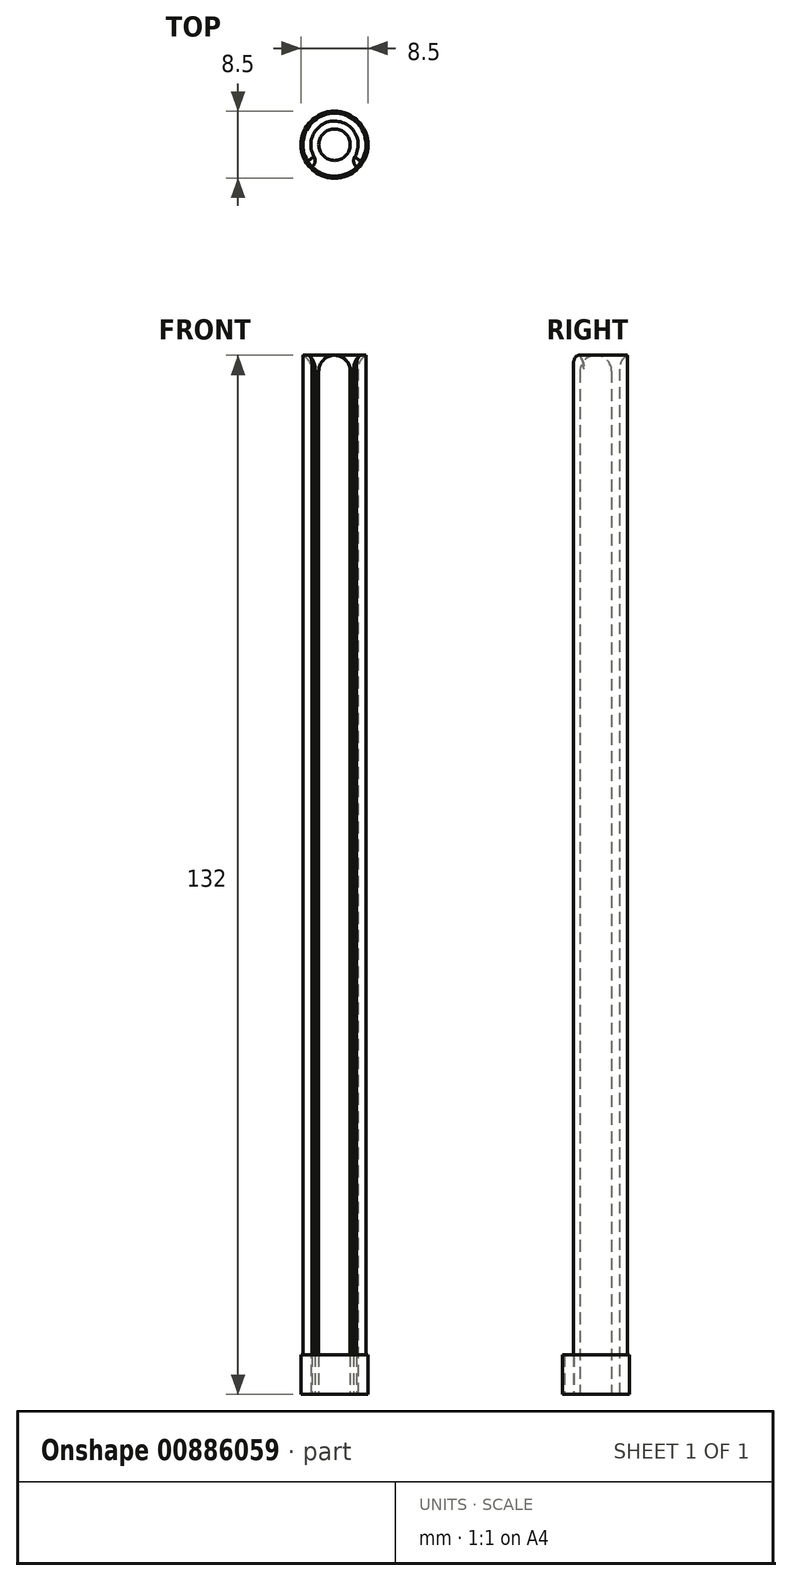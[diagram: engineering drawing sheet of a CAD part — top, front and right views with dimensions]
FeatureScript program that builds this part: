
annotation { "Feature Type Name" : "Feature", "Feature Type Description" : "" }
export const myFeature = defineFeature(function(context is Context, id is Id, definition is map)
    precondition{}
    {
        {
            var Q0;
            Q0=qCreatedBy(makeId("Top.planeOp"),FACE);
            var sketch = newSketch(context, id + "F0", { "sketchPlane" : qUnion([Q0])});
            skCircle(sketch, "E0", {"center": v(0, 0) * mm, "radius": 4.25 * mm});
            skCircle(sketch, "E1", {"center": v(0, 0) * mm, "radius": 4 * mm});
            skCircle(sketch, "E2", {"center": v(0, 0) * mm, "radius": 3 * mm});
            skLineSegment(sketch, "E3", {"start": v(-2.13, -2.1) * mm, "end": v(-2.85, -2.81) * mm});
            skLineSegment(sketch, "E4", {"start": v(2.1, -2.13) * mm, "end": v(2.81, -2.85) * mm});
            skCircle(sketch, "E5", {"center": v(0, 0) * mm, "radius": 2 * mm});
            skSolve(sketch);
        }
        {
            var Q0;
            Q0 = qSketchRegion(id + "F0", true);
            extrude(context, id + "F1", {"entities" : qUnion([Q0]), "depth" : 5 * mm, "offsetDistance" : 25 * mm});
        }
        {
            var Q0;
            {var subQ0=sQuery(id+"F0.wireOp",EDGE,"E3");Q0=makeQuery(id+"F0.imprint","IMPRINT",FACE,{"disambiguationData":[TD([[makeQuery(id+"F0.imprint","IMPRINT",EDGE,{"derivedFrom":subQ0}),-1.0]])]});}
            extrude(context, id + "F2", {"entities" : qUnion([Q0]), "operationType" : NewBodyOperationType.ADD, "depth" : 132 * mm, "offsetDistance" : 25 * mm});
        }
        {
            var Q0;
            Q0=makeQuery(id+"F0.imprint","IMPRINT",FACE,{"disambiguationData":[TD([[makeQuery(id+"F0.imprint","IMPRINT",EDGE,{"derivedFrom":sQuery(id+"F0.wireOp",EDGE,"E5")}),1.0]])]});
            extrude(context, id + "F3", {"entities" : qUnion([Q0]), "depth" : 132 * mm, "offsetDistance" : 25 * mm});
        }
        {
            var Q0;
            Q0=makeQuery(id+"F0.imprint","IMPRINT",FACE,{"disambiguationData":[TD([[makeQuery(id+"F0.imprint","IMPRINT",EDGE,{"derivedFrom":sQuery(id+"F0.wireOp",EDGE,"E0")}),1.0]])]});
            var Q1;
            {var subQ0=sQuery(id+"F0.wireOp",EDGE,"E3");Q1=makeQuery(id+"F0.imprint","IMPRINT",FACE,{"disambiguationData":[TD([[makeQuery(id+"F0.imprint","IMPRINT",EDGE,{"derivedFrom":subQ0}),1.0]])]});}
            var Q2;
            Q2=makeQuery(id+"F0.imprint","IMPRINT",FACE,{"disambiguationData":[TD([[makeQuery(id+"F0.imprint","IMPRINT",EDGE,{"derivedFrom":sQuery(id+"F0.wireOp",EDGE,"E5")}),-1.0]])]});
            var Q3;
            {var subQ0=sQuery(id+"F0.wireOp",EDGE,"E3");Q3=makeQuery(id+"F0.imprint","IMPRINT",FACE,{"disambiguationData":[TD([[makeQuery(id+"F0.imprint","IMPRINT",EDGE,{"derivedFrom":subQ0}),-1.0]])]});}
            var Q4;
            Q4=makeQuery(id+"F0.imprint","IMPRINT",FACE,{"disambiguationData":[TD([[makeQuery(id+"F0.imprint","IMPRINT",EDGE,{"derivedFrom":sQuery(id+"F0.wireOp",EDGE,"E5")}),1.0]])]});
            extrude(context, id + "F4", {"entities" : qUnion([Q0, Q1, Q2, Q3, Q4]), "depth" : 5 * mm, "offsetDistance" : 25 * mm});
        }
        {
            var Q0;
            Q0=makeQuery(id+"F3.opExtrude","CAP_EDGE",EDGE,{"disambiguationData":[OSD([sQuery(id+"F0.wireOp",EDGE,"E5")])],"isStart":false});
            var Q1;
            Q1=makeQuery(id+"F2.opExtrude","CAP_EDGE",EDGE,{"disambiguationData":[OSD([sQuery(id+"F0.wireOp",EDGE,"E2")])],"isStart":false});
            fillet(context, id + "F5", {"entities" : qUnion([Q0, Q1]), "radius" : 2 * mm, "tangentPropagation" : true, "allowEdgeOverflow" : false});
        }
        {
            var Q0;
            Q0=makeQuery(id+"F2.opExtrude","SWEPT_EDGE",EDGE,{"disambiguationData":[OSD([sQuery(id+"F0.wireOp",EDGE,"E2"),sQuery(id+"F0.wireOp",EDGE,"E4")])]});
            var Q1;
            Q1=makeQuery(id+"F2.opExtrude","SWEPT_EDGE",EDGE,{"disambiguationData":[OSD([sQuery(id+"F0.wireOp",EDGE,"E2"),sQuery(id+"F0.wireOp",EDGE,"E3")])]});
            fillet(context, id + "F6", {"entities" : qUnion([Q0, Q1]), "radius" : 1 * mm, "tangentPropagation" : true, "allowEdgeOverflow" : false});
        }
    });
